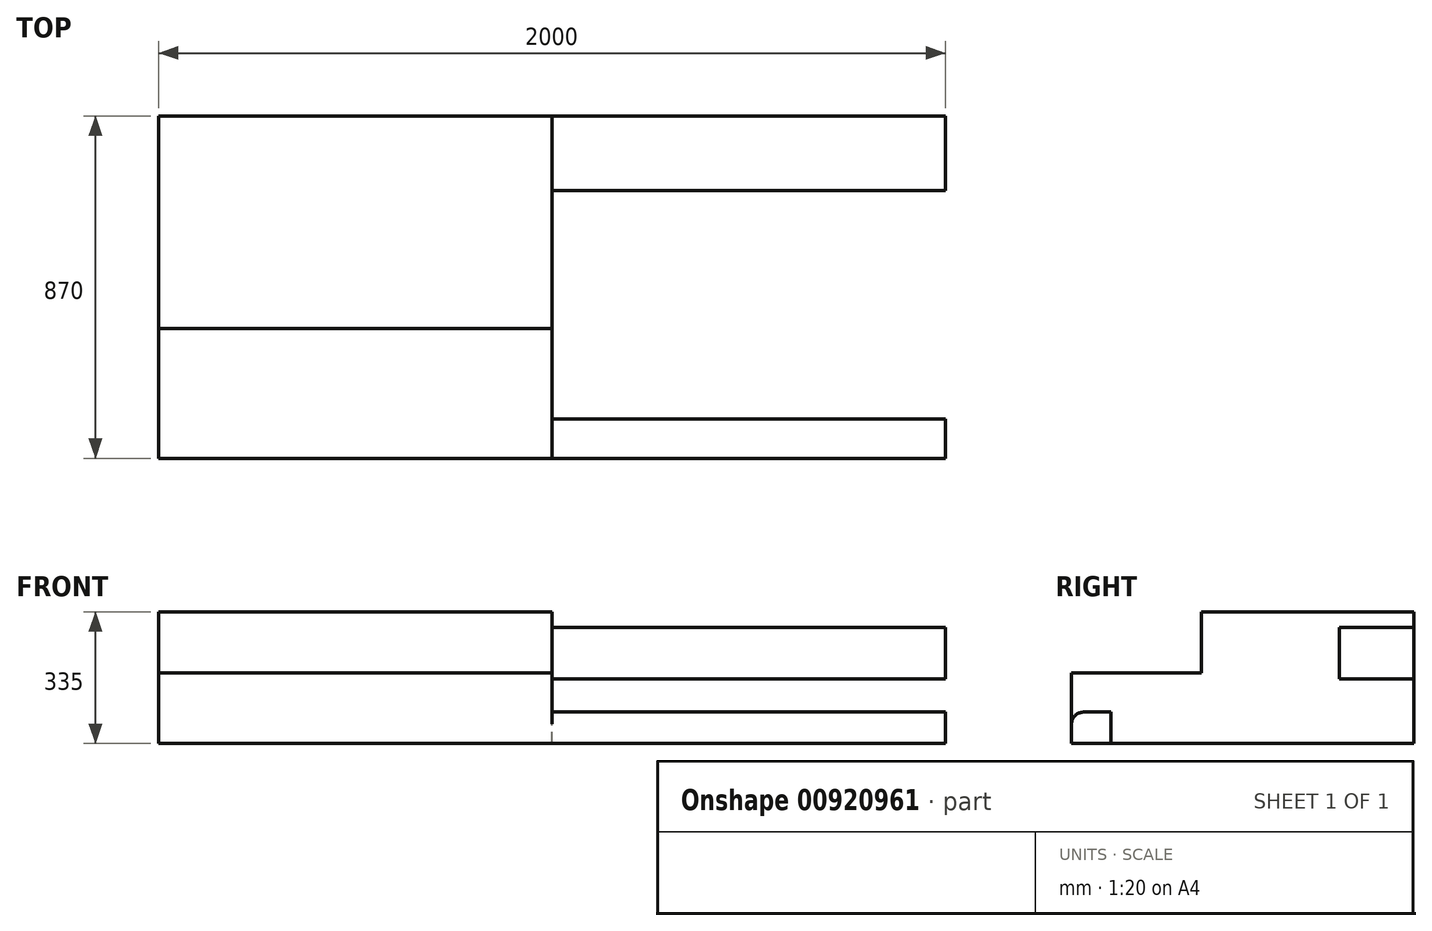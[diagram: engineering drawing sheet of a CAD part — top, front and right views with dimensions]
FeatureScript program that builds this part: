
annotation { "Feature Type Name" : "Feature", "Feature Type Description" : "" }
export const myFeature = defineFeature(function(context is Context, id is Id, definition is map)
    precondition{}
    {
        {
            var Q0;
            Q0=qCreatedBy(makeId("Top.planeOp"),FACE);
            var sketch = newSketch(context, id + "F0", { "sketchPlane" : qUnion([Q0])});
            skLineSegment(sketch, "E0.bottom", {"start": v(0, 0) * mm, "end": v(1000, 0) * mm});
            skLineSegment(sketch, "E0.top", {"start": v(0, -870) * mm, "end": v(1000, -870) * mm});
            skLineSegment(sketch, "E0.left", {"start": v(0, 0) * mm, "end": v(0, -870) * mm});
            skLineSegment(sketch, "E0.right", {"start": v(1000, 0) * mm, "end": v(1000, -870) * mm});
            skLineSegment(sketch, "E1.top", {"start": v(0, -540) * mm, "end": v(1000, -540) * mm});
            skLineSegment(sketch, "E1.left", {"start": v(0, 0) * mm, "end": v(0, -540) * mm});
            skLineSegment(sketch, "E1.right", {"start": v(1000, 0) * mm, "end": v(1000, -540) * mm});
            skSolve(sketch);
        }
        {
            var Q0;
            {var subQ0=sQuery(id+"F0.wireOp",EDGE,"E0.top");Q0=makeQuery(id+"F0.imprint","IMPRINT",FACE,{"disambiguationData":[TD([[makeQuery(id+"F0.imprint","IMPRINT",EDGE,{"derivedFrom":subQ0}),1.0]])]});}
            extrude(context, id + "F1", {"entities" : qUnion([Q0]), "depth" : 180 * mm, "offsetDistance" : 25 * mm});
        }
        {
            var Q0;
            {var subQ0=sQuery(id+"F0.wireOp",EDGE,"E0.bottom");Q0=makeQuery(id+"F0.imprint","IMPRINT",FACE,{"disambiguationData":[TD([[makeQuery(id+"F0.imprint","IMPRINT",EDGE,{"derivedFrom":subQ0}),-1.0]])]});}
            extrude(context, id + "F2", {"entities" : qUnion([Q0]), "operationType" : NewBodyOperationType.ADD, "depth" : 335 * mm, "offsetDistance" : 25 * mm});
        }
        {
            var Q0;
            {var subQ0=sQuery(id+"F0.wireOp",EDGE,"E0.right");Q0=makeQuery(id+"F2.boolean.opBoolean","MERGE",FACE,{"derivedFrom":[makeQuery(id+"F1.opExtrude","SWEPT_FACE",FACE,{"disambiguationData":[OSD([subQ0])]}),makeQuery(id+"F2.opExtrude","SWEPT_FACE",FACE,{"disambiguationData":[OSD([subQ0])]})]});}
            var sketch = newSketch(context, id + "F3", { "sketchPlane" : qUnion([Q0])});
            skLineSegment(sketch, "E2.top", {"start": v(0, 295) * mm, "end": v(-190, 295) * mm});
            skLineSegment(sketch, "E3.top", {"start": v(0, 165) * mm, "end": v(-190, 165) * mm});
            skLineSegment(sketch, "E3.left", {"start": v(0, 295) * mm, "end": v(0, 165) * mm});
            skLineSegment(sketch, "E3.right", {"start": v(-190, 295) * mm, "end": v(-190, 165) * mm});
            skLineSegment(sketch, "E4.bottom", {"start": v(-870, 0) * mm, "end": v(-770, 0) * mm});
            skLineSegment(sketch, "E4.top", {"start": v(-840, 80) * mm, "end": v(-770, 80) * mm});
            skLineSegment(sketch, "E4.left", {"start": v(-870, 0) * mm, "end": v(-870, 50) * mm});
            skLineSegment(sketch, "E4.right", {"start": v(-770, 0) * mm, "end": v(-770, 80) * mm});
            skPoint(sketch, "E5.visualSharp", {"position": v(-870, 80) * mm});
            skArc(sketch, "E5.filletArc", {"start": v(-840, 80) * mm, "mid": v(-861.21, 71.21) * mm, "end": v(-870, 50) * mm});
            skSolve(sketch);
        }
        {
            var Q0;
            Q0=makeQuery(id+"F3.imprint","IMPRINT",FACE,{"disambiguationData":[TD([[makeQuery(id+"F3.imprint","IMPRINT",EDGE,{"derivedFrom":sQuery(id+"F3.wireOp",EDGE,"E2.top")}),1.0]])]});
            extrude(context, id + "F4", {"entities" : qUnion([Q0]), "operationType" : NewBodyOperationType.ADD, "depth" : 1000 * mm, "offsetDistance" : 25 * mm});
        }
        {
            var Q0;
            {var subQ0=sQuery(id+"F0.wireOp",EDGE,"E0.right");Q0=makeQuery(id+"F2.boolean.opBoolean","MERGE",FACE,{"derivedFrom":[makeQuery(id+"F1.opExtrude","SWEPT_FACE",FACE,{"disambiguationData":[OSD([subQ0])]}),makeQuery(id+"F2.opExtrude","SWEPT_FACE",FACE,{"disambiguationData":[OSD([subQ0])]})]});}
            var sketch = newSketch(context, id + "F5", { "sketchPlane" : qUnion([Q0])});
            skSolve(sketch);
        }
        {
            var Q0;
            Q0 = qSketchRegion(id + "F3", true);
            extrude(context, id + "F6", {"entities" : qUnion([Q0]), "operationType" : NewBodyOperationType.ADD, "depth" : 1000 * mm, "offsetDistance" : 25 * mm});
        }
    });
